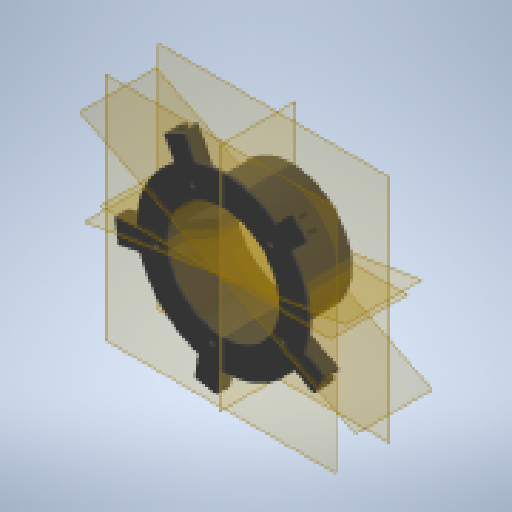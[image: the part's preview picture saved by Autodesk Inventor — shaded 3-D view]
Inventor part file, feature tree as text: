
AUTODESK INVENTOR PART (.ipt)
format: ipt  version: 2025.2 (Build 292293000, 293)  size: 502,784 bytes
history: native  units: mm
features: extrude x8, sketch x8, plane x4, fillet x3, mirror x2, pattern_circular x1, revolve x1, chamfer x1, projected_geometry x1
ambient origin geometry x8: Origin, YZ Plane, XZ Plane, XY Plane, X Axis, Y Axis, Z Axis, Center Point
bodies: Solid2 (feature_tree)
feature tree (29):
  extrude  "Extrusion6"  Depth=92.0mm
  extrude  "Extrusion8"  TaperAngle=45.0deg  [1 undecoded]
  sketch  "Sketch9"  dims[d30=2.75mm d31=0.0mm d32=45.0deg]
  extrude  "Extrusion7"  Depth=18.0mm
  extrude  "Extrusion9"  Depth=50.0mm TaperAngle=360.0deg
  plane  "Work Plane1"
  mirror  "Mirror1"
  extrude  "Extrusion11"  Depth=56.75mm TaperAngle=0.0deg
  extrude  "Extrusion10"  Depth=5.0mm
  fillet  "Fillet5"  Radius=4.5mm
  pattern_circular  "Circular Pattern1"  [2 undecoded]
  plane  "Work Plane2"
  plane  "Work Plane3"
  plane  "Work Plane4"
  extrude  "Extrusion12"  Depth=10.0mm
  revolve  "Revolution1"  [1 undecoded]
  extrude  "Extrusion14"  Depth=10.0mm TaperAngle=0.0deg
  mirror  "Mirror2"
  fillet  "Fillet6"  Radius=5.0mm
  chamfer  "Chamfer1"  [1 undecoded]
  fillet  "Fillet7"  Radius=26.0mm
  sketch  "Sketch8"  dims[d28=140.0mm d29=92.0mm]
  sketch  "Sketch10"  dims[d33=88.0mm d34=18.0mm]
  sketch  "Sketch11"  dims[d36=3.75mm d37=0.0mm d38=50.0mm d39=360.0deg]
  sketch  "Sketch12"  dims[d41=98.0mm d42=56.75mm d43=0.0mm]
  projected_geometry  "Projected Loop1"
  sketch  "Sketch13"  dims[d44=15.0mm d45=5.0mm d46=4.5mm]
  sketch  "Sketch14"  dims[d47=2.5mm]
  sketch  "Sketch15"  dims[d49=56.75mm d50=0.0mm d51=55.0mm d52=4.3mm d53=0.0mm d54=0.0mm d55=0.05mm d56=0.0mm d58=5.0mm d59=-44.75mm d60=26.0mm d61=31.75mm d62=29.25mm d63=0.0mm d64=15.0mm d67=3.0mm d68=10.0mm d69=5.0mm d72=13.0mm d75=6.0mm d77=5.0mm d78=11.25mm d79=8.0mm d80=2.5mm d81=3.0mm d82=14.0mm d83=0.0mm d84=7.0mm d85=15.0mm d86=2.0mm d87=45.0deg d88=10.0mm d89=45.0deg]
note: 5 required parameter values undecoded (feature->parameter linkage not recoverable at this tier; creation-order binding heuristic only, values carry confidence <= 0.55)